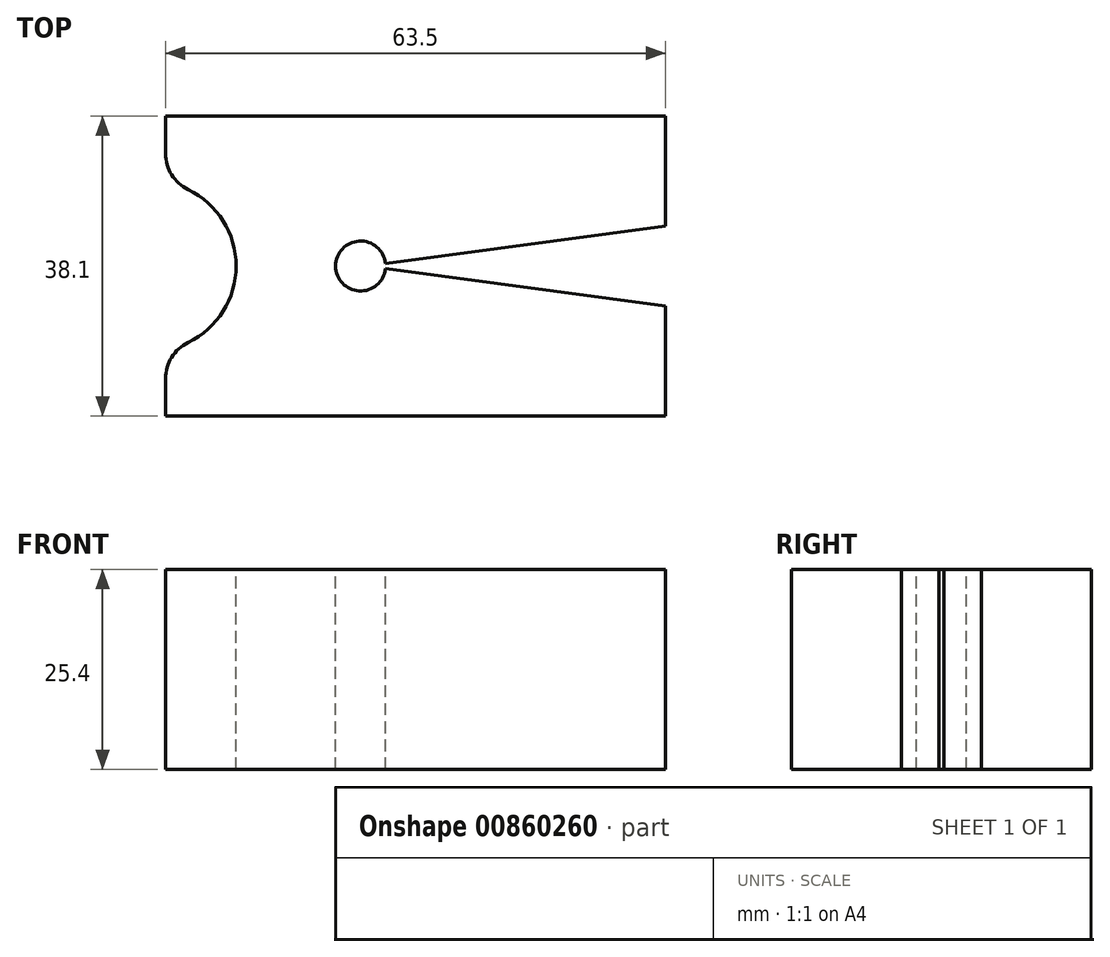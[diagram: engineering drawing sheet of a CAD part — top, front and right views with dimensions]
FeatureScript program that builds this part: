
annotation { "Feature Type Name" : "Feature", "Feature Type Description" : "" }
export const myFeature = defineFeature(function(context is Context, id is Id, definition is map)
    precondition{}
    {
        {
            var Q0;
            Q0=qCreatedBy(makeId("Top.planeOp"),FACE);
            var sketch = newSketch(context, id + "F0", { "sketchPlane" : qUnion([Q0])});
            skLineSegment(sketch, "E0.bottom", {"start": v(31.75, -19.05) * mm, "end": v(-31.75, -19.05) * mm});
            skLineSegment(sketch, "E0.top", {"start": v(31.75, 19.05) * mm, "end": v(-31.75, 19.05) * mm});
            skLineSegment(sketch, "E0.left", {"start": v(31.75, -19.05) * mm, "end": v(31.75, 19.05) * mm});
            skLineSegment(sketch, "E0.right", {"start": v(-31.75, -19.05) * mm, "end": v(-31.75, 19.05) * mm});
            skPoint(sketch, "E0.middle", {"position": v(0, 0) * mm});
            skSolve(sketch);
        }
        {
            var Q0;
            Q0=makeQuery(id+"F0.imprint","IMPRINT",FACE,{"disambiguationData":[TD([[makeQuery(id+"F0.imprint","IMPRINT",EDGE,{"derivedFrom":sQuery(id+"F0.wireOp",EDGE,"E0.bottom")}),-1.0]])]});
            extrude(context, id + "F1", {"entities" : qUnion([Q0]), "depth" : 25.4 * mm, "offsetDistance" : 25.4 * mm});
        }
        {
            var Q0;
            Q0=makeQuery(id+"F1.opExtrude","CAP_FACE",FACE,{"disambiguationData":[OSD([sQuery(id+"F0.wireOp",EDGE,"E0.bottom"),sQuery(id+"F0.wireOp",EDGE,"E0.top"),sQuery(id+"F0.wireOp",EDGE,"E0.left"),sQuery(id+"F0.wireOp",EDGE,"E0.right")])],"isStart":false});
            var sketch = newSketch(context, id + "F2", { "sketchPlane" : qUnion([Q0])});
            skSolve(sketch);
        }
        {
            var Q0;
            {var subQ3=sQuery(id+"F0.wireOp",EDGE,"E0.bottom");Q0=makeQuery(id+"F2.imprint","IMPRINT",FACE,{"disambiguationData":[TD([[makeQuery(id+"F2.imprint","IMPRINT",EDGE,{"derivedFrom":makeQuery(id+"F1.opExtrude","CAP_EDGE",EDGE,{"disambiguationData":[OSD([subQ3])],"isStart":false})}),-1.0]])]});}
            var sketch = newSketch(context, id + "F3", { "sketchPlane" : qUnion([Q0])});
            skLineSegment(sketch, "E1", {"start": v(-6.35, 0) * mm, "end": v(31.75, 5.08) * mm});
            skLineSegment(sketch, "E2", {"start": v(31.75, 5.08) * mm, "end": v(31.75, -5.08) * mm});
            skLineSegment(sketch, "E3", {"start": v(31.75, -5.08) * mm, "end": v(-6.35, 0) * mm});
            skCircle(sketch, "E4", {"center": v(-6.99, 0) * mm, "radius": 3.18 * mm});
            skSolve(sketch);
        }
        {
            var Q0;
            Q0 = qSketchRegion(id + "F3", true);
            extrude(context, id + "F4", {"entities" : qUnion([Q0]), "operationType" : NewBodyOperationType.REMOVE, "oppositeDirection" : true, "depth" : 38.1 * mm, "offsetDistance" : 25.4 * mm});
        }
        {
            var Q0;
            Q0=makeQuery(id+"F2.imprint","IMPRINT",FACE,{"disambiguationData":[TD([[makeQuery(id+"F2.imprint","IMPRINT",EDGE,{"derivedFrom":makeQuery(id+"F1.opExtrude","CAP_EDGE",EDGE,{"disambiguationData":[OSD([sQuery(id+"F0.wireOp",EDGE,"E0.bottom")])],"isStart":false})}),-1.0]])]});
            var sketch = newSketch(context, id + "F5", { "sketchPlane" : qUnion([Q0])});
            skCircle(sketch, "E5", {"center": v(-33.59, 0) * mm, "radius": 10.8 * mm});
            skSolve(sketch);
        }
        {
            var Q0;
            Q0 = qSketchRegion(id + "F5", true);
            extrude(context, id + "F6", {"entities" : qUnion([Q0]), "operationType" : NewBodyOperationType.REMOVE, "oppositeDirection" : true, "depth" : 38.1 * mm, "offsetDistance" : 25.4 * mm});
        }
        {
            var Q0;
            Q0=makeQuery(id+"F6.boolean.opBoolean","INTERSECT",EDGE,{"disambiguationData":[OD(1.0)],"derivedFrom":[makeQuery(id+"F1.opExtrude","SWEPT_FACE",FACE,{"disambiguationData":[OSD([sQuery(id+"F0.wireOp",EDGE,"E0.right")])]}),makeQuery(id+"F6.opExtrude","SWEPT_FACE",FACE,{"disambiguationData":[OSD([sQuery(id+"F5.wireOp",EDGE,"E5")])]})]});
            var Q1;
            Q1=makeQuery(id+"F6.boolean.opBoolean","INTERSECT",EDGE,{"disambiguationData":[OD(0.0)],"derivedFrom":[makeQuery(id+"F1.opExtrude","SWEPT_FACE",FACE,{"disambiguationData":[OSD([sQuery(id+"F0.wireOp",EDGE,"E0.right")])]}),makeQuery(id+"F6.opExtrude","SWEPT_FACE",FACE,{"disambiguationData":[OSD([sQuery(id+"F5.wireOp",EDGE,"E5")])]})]});
            fillet(context, id + "F7", {"entities" : qUnion([Q0, Q1]), "radius" : 5.08 * mm, "tangentPropagation" : true, "allowEdgeOverflow" : false});
        }
    });
